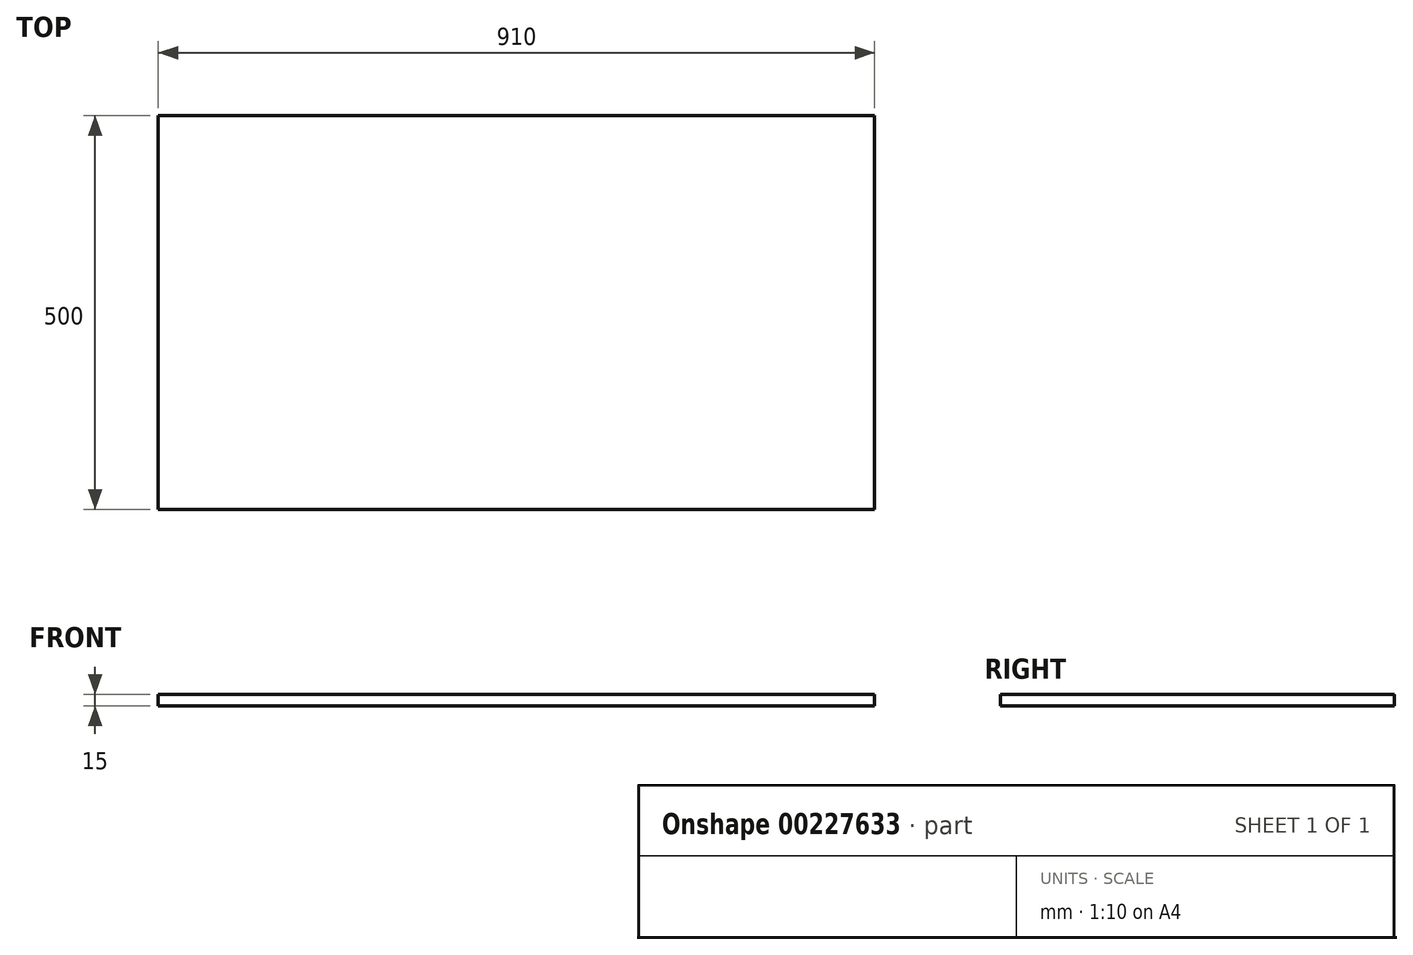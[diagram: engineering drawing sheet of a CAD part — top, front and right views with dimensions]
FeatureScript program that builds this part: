
annotation { "Feature Type Name" : "Feature", "Feature Type Description" : "" }
export const myFeature = defineFeature(function(context is Context, id is Id, definition is map)
    precondition{}
    {
        {
            var Q0;
            Q0=qCreatedBy(makeId("Front.planeOp"),FACE);
            var sketch = newSketch(context, id + "F0", { "sketchPlane" : qUnion([Q0])});
            skLineSegment(sketch, "E0.bottom", {"start": v(-241.52, -32.89) * mm, "end": v(668.48, -32.89) * mm});
            skLineSegment(sketch, "E0.top", {"start": v(-241.52, -47.89) * mm, "end": v(668.48, -47.89) * mm});
            skLineSegment(sketch, "E0.left", {"start": v(-241.52, -32.89) * mm, "end": v(-241.52, -47.89) * mm});
            skLineSegment(sketch, "E0.right", {"start": v(668.48, -32.89) * mm, "end": v(668.48, -47.89) * mm});
            skSolve(sketch);
        }
        {
            var Q0;
            Q0=makeQuery(id+"F0.imprint","IMPRINT",FACE,{"disambiguationData":[TD([[makeQuery(id+"F0.imprint","IMPRINT",EDGE,{"derivedFrom":sQuery(id+"F0.wireOp",EDGE,"E0.bottom")}),-1.0]])]});
            extrude(context, id + "F1", {"entities" : qUnion([Q0]), "oppositeDirection" : true, "depth" : 500 * mm});
        }
    });
